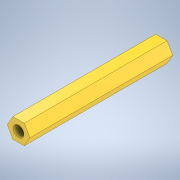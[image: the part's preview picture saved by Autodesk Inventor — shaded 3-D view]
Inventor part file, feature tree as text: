
AUTODESK INVENTOR PART (.ipt)
format: ipt  version: 2020 (Build 240168000, 168)  size: 101,376 bytes
history: native  units: mm
features: extrude x1, sketch x1
ambient origin geometry x8: Origin, YZ Plane, XZ Plane, XY Plane, X Axis, Y Axis, Z Axis, Center Point
bodies: Solid1 (feature_tree)
feature tree (2):
  extrude  "Extrusion1"  Depth=40.0mm
  sketch  "Sketch1"  dims[d0=5.5mm d1=3.0mm d2=40.0mm d3=0.0mm]
